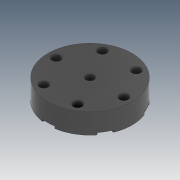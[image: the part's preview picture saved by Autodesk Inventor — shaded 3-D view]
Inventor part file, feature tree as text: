
AUTODESK INVENTOR PART (.ipt)
format: ipt  version: 2020 (Build 240168000, 168)  size: 248,832 bytes
history: native  units: mm
features: sketch x4, fillet x3, revolve x2, extrude x2, pattern_circular x2, thicken_offset x1, chamfer x1
ambient origin geometry x8: Origin, YZ Plane, XZ Plane, XY Plane, X Axis, Y Axis, Z Axis, Center Point
bodies: Solid1 (feature_tree)
feature tree (15):
  revolve  "Revolution1"  [1 undecoded]
  extrude  "Extrusion1"  Depth=6.5mm
  pattern_circular  "Circular Pattern1"  Count=6 Angle=360.0deg
  revolve  "Revolution2"  [1 undecoded]
  thicken_offset  "Thicken1"
  fillet  "Fillet1"  Radius=2.2mm
  fillet  "Fillet2"  Radius=7.0mm
  extrude  "Extrusion3"  TaperAngle=90.0deg  [1 undecoded]
  chamfer  "Chamfer1"  Distance=6.0mm
  fillet  "Fillet3"  Radius=6.0mm
  pattern_circular  "Circular Pattern2"  [2 undecoded]
  sketch  "Sketch1"  dims[d0=19.0mm d1=1.5mm d2=2.0mm d3=5.0mm d4=90.0deg d6=2.0mm d7=12.0mm d8=5.0mm d9=9.0mm]
  sketch  "Sketch2"  dims[d10=90.0deg d11=6.5mm]
  sketch  "Sketch4"  dims[d12=10.0mm d13=0.0mm d14=60.0mm d15=360.0deg]
  sketch  "Sketch5"  dims[d21=4.0mm d22=3.05mm d23=2.2mm d24=7.0mm d25=90.0deg d26=6.0mm d27=6.0mm d28=2.0mm d29=0.5mm d30=1.396263mm d31=3.5mm d32=1.5mm d33=0.0mm d34=1.5mm d35=3.5mm d36=45.0deg d37=0.5mm d38=60.0mm d39=360.0deg]
note: 5 required parameter values undecoded (feature->parameter linkage not recoverable at this tier; creation-order binding heuristic only, values carry confidence <= 0.55)